# Revit family: NLRS_57_AIR_UN_grated-wall-grill-hrec_LT_sacs
name_source: partatom
category: Air Terminals
units: mm (PartAtom-declared; Revit-internal decimal feet)

## family parameters
Always vertical = Yes
Cut with Voids When Loaded = No
Part Type = Normal
Room Calculation Point = Yes
Round Connector Dimension = Use Diameter
Shared = No
Work Plane-Based = No

## types (2) — shared parameters
Assembly Code = 57.00
Description = Wall grill for return air
IfcDescription = Wall grill for return air
IfcExportAs = IfcAirTerminal
IfcExportType = DIFFUSER
Manufacturer = Solid Air Climate Solutions
NLRS_C_content_datum_uitgifte = 11-08-2025
NLRS_C_content_provider = Solid Air Climate Solutions
NLRS_C_content_versie = 4.22.01
NLRS_C_description = Wall grill for return air
SACS_Data_Hidden = HREC_Wand
SACS_Data_Hidden2 = HREC_Factors
URL = https://solid-air.nl
zero-valued in all types: Default Elevation

## per-type parameters (varying)
| type | SACS_Base_Index |
| HRECOZ wand | 0 |
| HRECVZ wand | 1 |

## geometry (parser evidence)
native form markers: Sweep x11
no freeform markers — native parametric forms only
